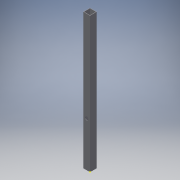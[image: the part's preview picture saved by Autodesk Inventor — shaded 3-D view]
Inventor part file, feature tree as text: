
AUTODESK INVENTOR PART (.ipt)
format: ipt  version: 2016 (Build 200138000, 138)  size: 139,776 bytes
history: native  units: in
note: dims shown in document units (in); Inventor stores cm internally (conversion verified against a paired STEP export)
features: sketch x7, extrude x6
ambient origin geometry x8: Origin, YZ Plane, XZ Plane, XY Plane, X Axis, Y Axis, Z Axis, Center Point
bodies: Solid1 (feature_tree)
feature tree (13):
  extrude  "Extrusion1"  Depth=1.0in
  sketch  "Sketch3"  dims[d2=0.0625in d3=20.0in d4=0.0in]
  extrude  "Extrusion3"  Depth=0.0625in TaperAngle=0.0deg
  extrude  "Extrusion4"  Depth=6.63in
  extrude  "Extrusion5"  Depth=1.0in
  extrude  "Extrusion6"  Depth=1.0in
  extrude  "Extrusion7"  Depth=3.3in
  sketch  "Sketch1"  dims[d0=1.0in d1=1.0in]
  sketch  "Sketch4"  dims[d8=0.5in d9=6.63in]
  sketch  "Sketch5"  dims[d10=1.0in d11=0.0in d12=0.5in]
  sketch  "Sketch6"  dims[d13=1.0in d14=0.0in d15=6.64in]
  sketch  "Sketch7"  dims[d16=0.5in d17=3.3in]
  sketch  "Sketch8"  dims[d18=0.401in d19=1.0in d20=0.0in d21=1.0in d22=0.0in d23=0.5in d24=0.485in d25=1.0in d26=0.0in]
